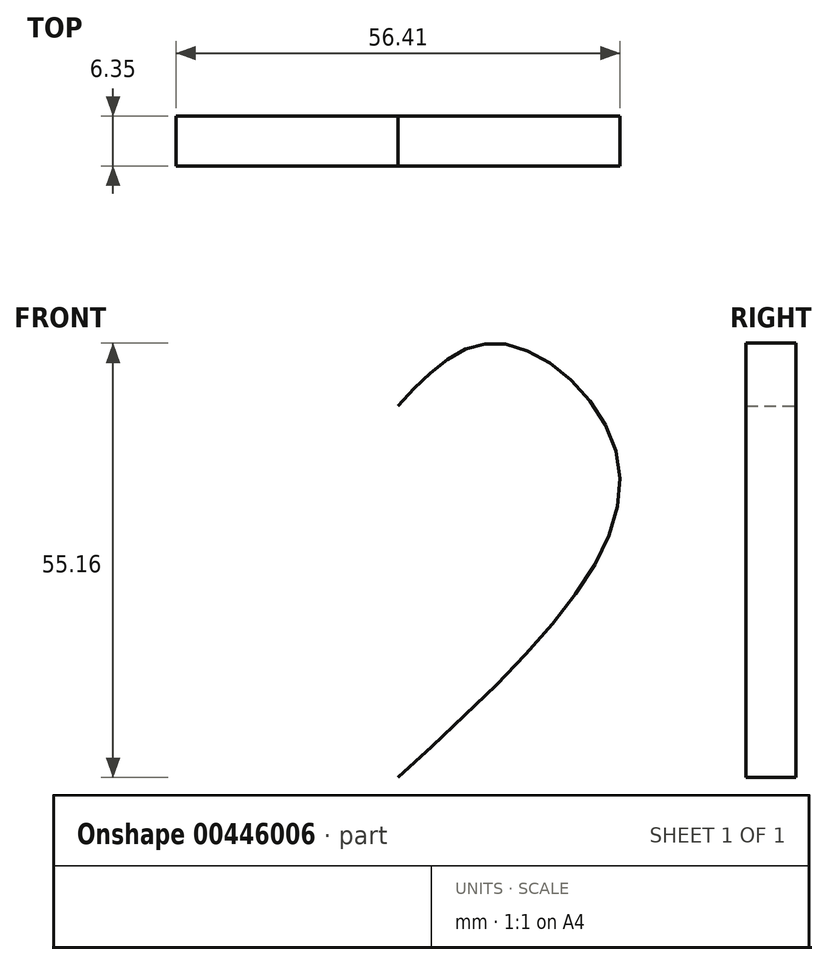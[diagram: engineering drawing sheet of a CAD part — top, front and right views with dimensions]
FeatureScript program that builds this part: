
annotation { "Feature Type Name" : "Feature", "Feature Type Description" : "" }
export const myFeature = defineFeature(function(context is Context, id is Id, definition is map)
    precondition{}
    {
        {
            var Q0;
            Q0=qCreatedBy(makeId("Front.planeOp"),FACE);
            var sketch = newSketch(context, id + "F0", { "sketchPlane" : qUnion([Q0])});
            skFitSpline(sketch, "E0", {"points": [v(-4.54, 17.44) * mm, v(-17.56, 25.35) * mm, v(-32.68, 9.07) * mm, v(-4.54, -29.77) * mm], "startDerivative": vector(-46.86, 50.28) * mm, "endDerivative": vector(98.58, -90.38) * mm});
            skFitSpline(sketch, "E1.MirrorCS", {"points": [v(-4.54, 17.44) * mm, v(8.49, 25.35) * mm, v(23.6, 9.07) * mm, v(-4.54, -29.77) * mm], "startDerivative": vector(46.86, 50.28) * mm, "endDerivative": vector(-98.58, -90.38) * mm});
            skSolve(sketch);
        }
        {
            var Q0;
            Q0 = qSketchRegion(id + "F0", true);
            extrude(context, id + "F1", {"entities" : qUnion([Q0]), "depth" : 6.35 * mm});
        }
    });
